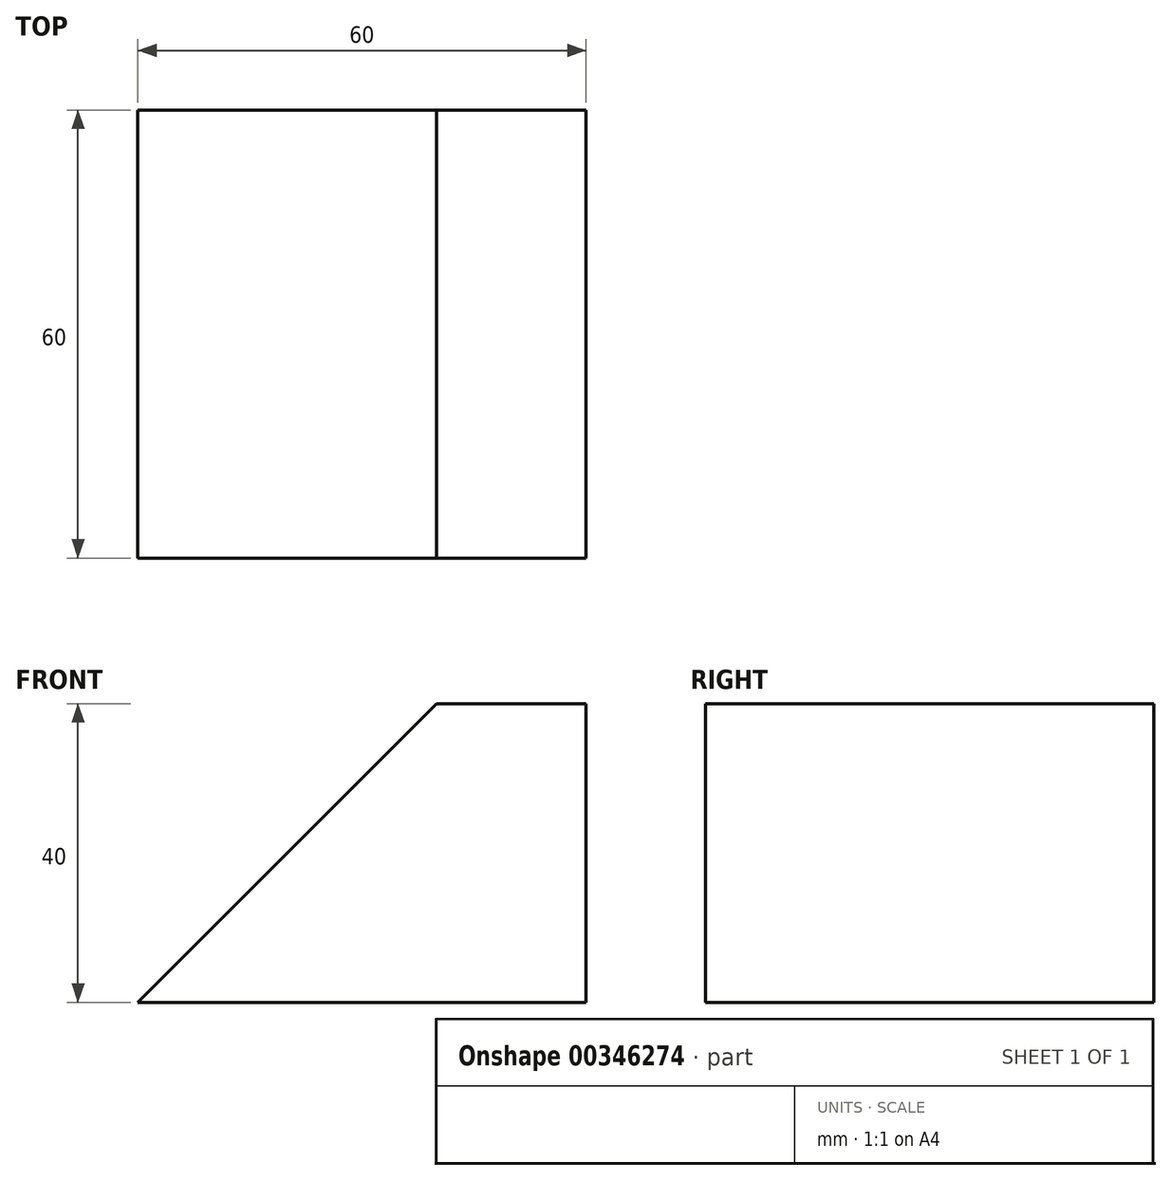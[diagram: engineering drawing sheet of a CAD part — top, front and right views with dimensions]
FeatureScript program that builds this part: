
annotation { "Feature Type Name" : "Feature", "Feature Type Description" : "" }
export const myFeature = defineFeature(function(context is Context, id is Id, definition is map)
    precondition{}
    {
        {
            var Q0;
            Q0=qCreatedBy(makeId("Front.planeOp"),FACE);
            var sketch = newSketch(context, id + "F0", { "sketchPlane" : qUnion([Q0])});
            skLineSegment(sketch, "E0", {"start": v(0, 0) * mm, "end": v(40, 40) * mm});
            skLineSegment(sketch, "E1", {"start": v(40, 40) * mm, "end": v(60, 40) * mm});
            skLineSegment(sketch, "E2", {"start": v(60, 40) * mm, "end": v(60, 0) * mm});
            skLineSegment(sketch, "E3", {"start": v(60, 0) * mm, "end": v(0, 0) * mm});
            skLineSegment(sketch, "E4", {"start": v(0, 0) * mm, "end": v(20, 30) * mm});
            skLineSegment(sketch, "E5", {"start": v(20, 30) * mm, "end": v(40, 40) * mm});
            skSolve(sketch);
        }
        {
            var Q0;
            Q0=makeQuery(id+"F0.imprint","IMPRINT",FACE,{"disambiguationData":[TD([[makeQuery(id+"F0.imprint","IMPRINT",EDGE,{"derivedFrom":sQuery(id+"F0.wireOp",EDGE,"E0")}),-1.0]])]});
            extrude(context, id + "F1", {"entities" : qUnion([Q0]), "depth" : 30 * mm, "hasSecondDirection" : true, "secondDirectionOppositeDirection" : true, "secondDirectionDepth" : 30 * mm});
        }
        {
            var Q0;
            Q0=makeQuery(id+"F1.opExtrude","SWEPT_FACE",FACE,{"disambiguationData":[OSD([sQuery(id+"F0.wireOp",EDGE,"E0")])]});
            var sketch = newSketch(context, id + "F2", { "sketchPlane" : qUnion([Q0])});
            skLineSegment(sketch, "E6", {"start": v(-30, 0) * mm, "end": v(0, 56.57) * mm});
            skLineSegment(sketch, "E7", {"start": v(0, 56.57) * mm, "end": v(30, 0) * mm});
            skLineSegment(sketch, "E8", {"start": v(30, 0) * mm, "end": v(-30, 0) * mm});
            skSolve(sketch);
        }
    });
